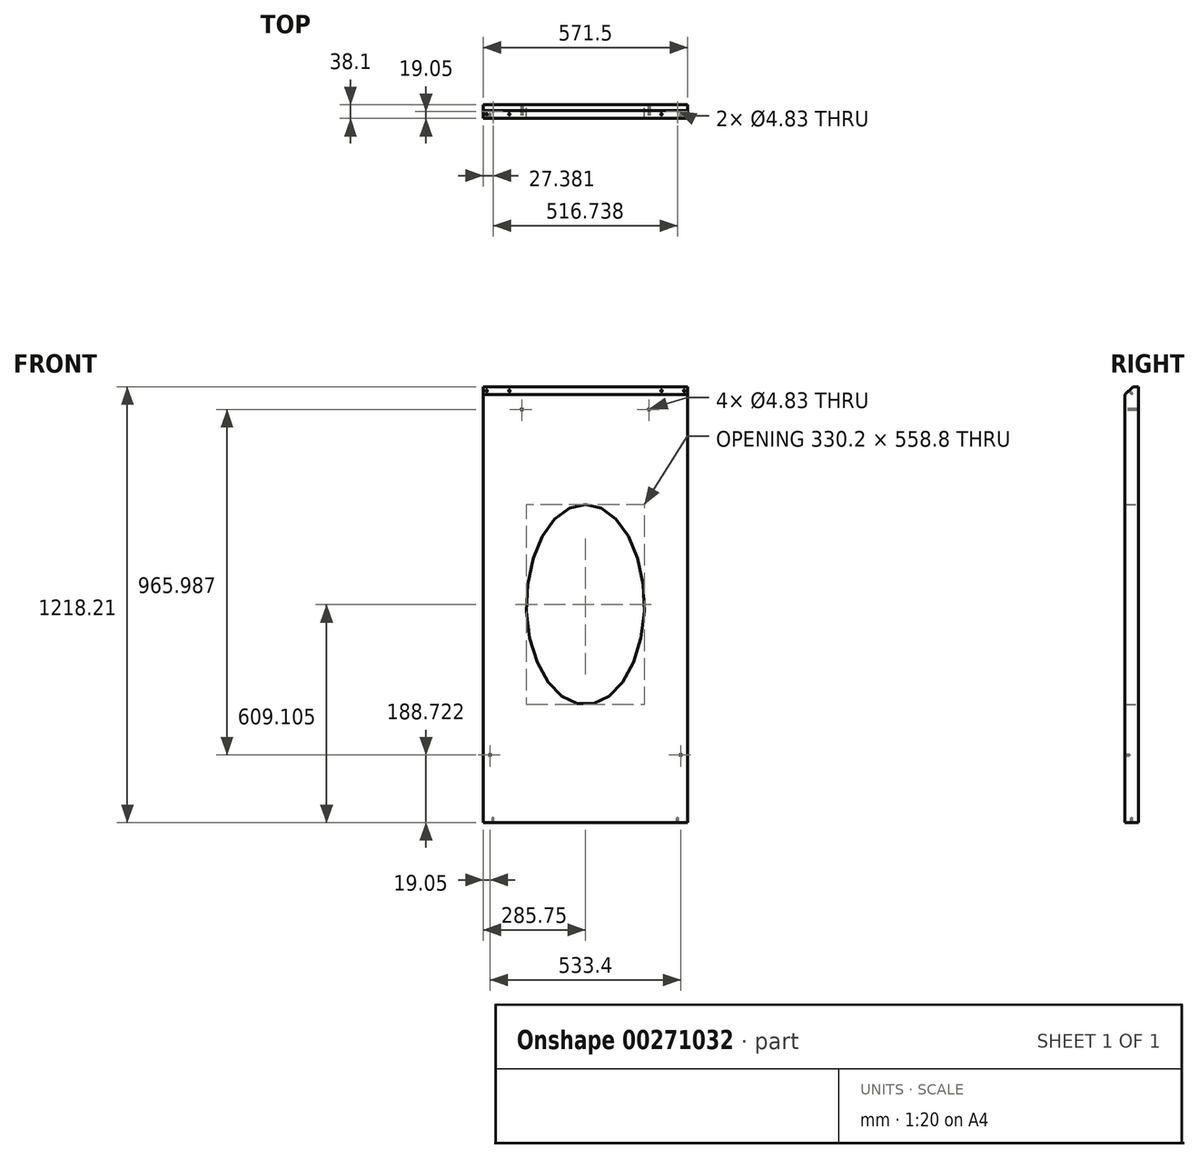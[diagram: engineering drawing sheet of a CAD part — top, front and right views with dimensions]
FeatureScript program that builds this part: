
annotation { "Feature Type Name" : "Feature", "Feature Type Description" : "" }
export const myFeature = defineFeature(function(context is Context, id is Id, definition is map)
    precondition{}
    {
        {
            var Q0;
            Q0=qCreatedBy(makeId("Front.planeOp"),FACE);
            var sketch = newSketch(context, id + "F0", { "sketchPlane" : qUnion([Q0])});
            skLineSegment(sketch, "E0.bottom", {"start": v(0, 0) * mm, "end": v(571.5, 0) * mm});
            skLineSegment(sketch, "E0.top", {"start": v(0, 1218.2) * mm, "end": v(571.5, 1218.2) * mm});
            skLineSegment(sketch, "E0.left", {"start": v(0, 0) * mm, "end": v(0, 1218.2) * mm});
            skLineSegment(sketch, "E0.right", {"start": v(571.5, 0) * mm, "end": v(571.5, 1218.2) * mm});
            skEllipse(sketch, "E1", {"center": v(285.75, 609.1) * mm, "majorRadius": 279.4 * mm, "minorRadius": 165.1 * mm, "majorAxis": v(0, 1)});
            skPoint(sketch, "E1.centerSnap0", {"position": v(0, 609.1) * mm});
            skPoint(sketch, "E1.centerSnap1", {"position": v(285.75, 1218.2) * mm});
            skSolve(sketch);
        }
        {
            var Q0;
            Q0 = qSketchRegion(id + "F0", true);
            extrude(context, id + "F1", {"entities" : qUnion([Q0]), "depth" : 38.1 * mm});
        }
        {
            var Q0;
            Q0=makeQuery(id+"F1.opExtrude","CAP_EDGE",EDGE,{"disambiguationData":[OSD([sQuery(id+"F0.wireOp",EDGE,"E0.top")])],"isStart":false});
            chamfer(context, id + "F2", {"entities" : qUnion([Q0]), "chamferType" : ChamferType.OFFSET_ANGLE, "width" : 22.22 * mm, "oppositeDirection" : false, "angle" : 45 * degree, "tangentPropagation" : true});
        }
        {
            var Q0;
            Q0=makeQuery(id+"F1.opExtrude","CAP_FACE",FACE,{"disambiguationData":[OSD([sQuery(id+"F0.wireOp",EDGE,"E0.bottom"),sQuery(id+"F0.wireOp",EDGE,"E0.top"),sQuery(id+"F0.wireOp",EDGE,"E0.left"),sQuery(id+"F0.wireOp",EDGE,"E0.right"),sQuery(id+"F0.wireOp",EDGE,"E1")])],"isStart":true});
            var sketch = newSketch(context, id + "F3", { "sketchPlane" : qUnion([Q0])});
            skPoint(sketch, "E2", {"position": v(-463.55, 1154.7) * mm});
            skPoint(sketch, "E3", {"position": v(-107.95, 1154.7) * mm});
            skSolve(sketch);
        }
        {
            var Q0;
            Q0=sQuery(id+"F3.wireOp",VERTEX,"E2");
            var Q1;
            Q1=sQuery(id+"F3.wireOp",VERTEX,"E3");
            var Q2;
            Q2=makeQuery(id+"F1.opExtrude","SWEPT_BODY",BODY,{"disambiguationData":[OSD([sQuery(id+"F0.wireOp",EDGE,"E0.bottom"),sQuery(id+"F0.wireOp",EDGE,"E0.top"),sQuery(id+"F0.wireOp",EDGE,"E0.left"),sQuery(id+"F0.wireOp",EDGE,"E0.right"),sQuery(id+"F0.wireOp",EDGE,"E1")])]});
            hole(context, id + "F4", {"style" : HoleStyle.SIMPLE, "endStyle" : HoleEndStyle.THROUGH, "holeDiameter" : 4.83 * mm, "tappedDepth" : 12.7 * mm, "tapClearance" : 3, "locations" : qUnion([Q0, Q1]), "scope" : qUnion([Q2])});
        }
        {
            var Q0;
            Q0=makeQuery(id+"F2.opChamfer","BLEND_FACE",FACE,{"disambiguationData":[OSD([sQuery(id+"F0.wireOp",EDGE,"E0.top")])]});
            var sketch = newSketch(context, id + "F5", { "sketchPlane" : qUnion([Q0])});
            skPoint(sketch, "E4", {"position": v(9.53, 834.46) * mm});
            skPoint(sketch, "E4.positionSnap0", {"position": v(0, 834.46) * mm});
            skPoint(sketch, "E5", {"position": v(73.03, 834.46) * mm});
            skPoint(sketch, "E6", {"position": v(561.97, 834.46) * mm});
            skPoint(sketch, "E6.positionSnap0", {"position": v(571.5, 834.46) * mm});
            skPoint(sketch, "E7", {"position": v(498.47, 834.46) * mm});
            skSolve(sketch);
        }
        {
            var Q0;
            Q0=makeQuery(id+"F1.opExtrude","CAP_FACE",FACE,{"disambiguationData":[OSD([sQuery(id+"F0.wireOp",EDGE,"E0.bottom"),sQuery(id+"F0.wireOp",EDGE,"E0.top"),sQuery(id+"F0.wireOp",EDGE,"E0.left"),sQuery(id+"F0.wireOp",EDGE,"E0.right"),sQuery(id+"F0.wireOp",EDGE,"E1")])],"isStart":false});
            var sketch = newSketch(context, id + "F6", { "sketchPlane" : qUnion([Q0])});
            skPoint(sketch, "E8", {"position": v(552.45, 188.72) * mm});
            skPoint(sketch, "E9", {"position": v(19.05, 188.72) * mm});
            skSolve(sketch);
        }
        {
            var Q0;
            Q0=sQuery(id+"F5.wireOp",VERTEX,"E4");
            var Q1;
            Q1=sQuery(id+"F5.wireOp",VERTEX,"E5");
            var Q2;
            Q2=sQuery(id+"F5.wireOp",VERTEX,"E7");
            var Q3;
            Q3=sQuery(id+"F5.wireOp",VERTEX,"E6");
            var Q4;
            Q4=sQuery(id+"F6.wireOp",VERTEX,"E9");
            var Q5;
            Q5=sQuery(id+"F6.wireOp",VERTEX,"E8");
            var Q6;
            Q6=makeQuery(id+"F1.opExtrude","SWEPT_BODY",BODY,{"disambiguationData":[OSD([sQuery(id+"F0.wireOp",EDGE,"E0.bottom"),sQuery(id+"F0.wireOp",EDGE,"E0.top"),sQuery(id+"F0.wireOp",EDGE,"E0.left"),sQuery(id+"F0.wireOp",EDGE,"E0.right"),sQuery(id+"F0.wireOp",EDGE,"E1")])]});
            hole(context, id + "F7", {"style" : HoleStyle.SIMPLE, "endStyle" : HoleEndStyle.BLIND, "holeDiameter" : 4.83 * mm, "holeDepth" : 12.7 * mm, "tappedDepth" : 12.7 * mm, "tapClearance" : 3, "locations" : qUnion([Q0, Q1, Q2, Q3, Q4, Q5]), "scope" : qUnion([Q6])});
        }
        {
            var Q0;
            Q0=makeQuery(id+"F1.opExtrude","SWEPT_FACE",FACE,{"disambiguationData":[OSD([sQuery(id+"F0.wireOp",EDGE,"E0.bottom")])]});
            var sketch = newSketch(context, id + "F8", { "sketchPlane" : qUnion([Q0])});
            skPoint(sketch, "E10", {"position": v(27.38, 19.05) * mm});
            skPoint(sketch, "E10.positionSnap0", {"position": v(0, 19.05) * mm});
            skPoint(sketch, "E11", {"position": v(544.12, 19.05) * mm});
            skSolve(sketch);
        }
        {
            var Q0;
            Q0=sQuery(id+"F8.wireOp",VERTEX,"E10");
            var Q1;
            Q1=sQuery(id+"F8.wireOp",VERTEX,"E11");
            var Q2;
            Q2=makeQuery(id+"F1.opExtrude","SWEPT_BODY",BODY,{"disambiguationData":[OSD([sQuery(id+"F0.wireOp",EDGE,"E0.bottom"),sQuery(id+"F0.wireOp",EDGE,"E0.top"),sQuery(id+"F0.wireOp",EDGE,"E0.left"),sQuery(id+"F0.wireOp",EDGE,"E0.right"),sQuery(id+"F0.wireOp",EDGE,"E1")])]});
            hole(context, id + "F9", {"style" : HoleStyle.SIMPLE, "endStyle" : HoleEndStyle.BLIND, "holeDiameter" : 4.83 * mm, "holeDepth" : 12.7 * mm, "tappedDepth" : 12.7 * mm, "tapClearance" : 3, "locations" : qUnion([Q0, Q1]), "scope" : qUnion([Q2])});
        }
    });
